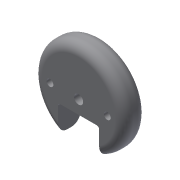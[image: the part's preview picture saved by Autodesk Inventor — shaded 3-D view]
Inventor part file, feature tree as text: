
AUTODESK INVENTOR PART (.ipt)
format: ipt  version: 2015 (Build 190159000, 159)  size: 184,320 bytes
history: native  units: mm
features: sketch x12, extrude x10, fillet x2
ambient origin geometry x8: Origin, YZ Plane, XZ Plane, XY Plane, X Axis, Y Axis, Z Axis, Center Point
bodies: Solid1 (feature_tree)
feature tree (24):
  extrude  "Extrusion1"  Depth=10.0mm TaperAngle=0.0deg
  extrude  "Extrusion2"  Depth=10.0mm TaperAngle=0.0deg
  extrude  "Extrusion3"  Depth=3.0mm
  sketch  "Sketch4"  dims[d9=10.0mm d10=0.0mm d11=10.0mm]
  sketch  "Sketch5"  dims[d12=10.0mm d13=0.0mm d14=6.0mm]
  extrude  "Extrusion4"  Depth=10.0mm
  extrude  "Extrusion5"  Depth=6.0mm
  extrude  "Extrusion6"  Depth=18.0mm
  extrude  "Extrusion7"  Depth=10.0mm TaperAngle=0.0deg
  extrude  "Extrusion8"  Depth=2.0mm
  extrude  "Extrusion9"  Depth=8.0mm TaperAngle=0.0deg
  extrude  "Extrusion10"  Depth=4.0mm
  fillet  "Fillet1"  Radius=10.0mm
  fillet  "Fillet2"  Radius=1.0mm
  sketch  "Sketch1"  dims[d0=40.0mm d1=10.0mm d2=0.0mm]
  sketch  "Sketch2"  dims[d3=12.0mm d4=10.0mm d5=0.0mm]
  sketch  "Sketch3"  dims[d7=3.0mm d8=3.0mm]
  sketch  "Sketch6"  dims[d15=2.0mm d16=0.0mm d17=18.0mm]
  sketch  "Sketch7"  dims[d18=10.0mm d19=10.0mm d20=0.0mm]
  sketch  "Sketch8"  dims[d21=18.0mm d25=2.0mm]
  sketch  "Sketch9"  dims[d26=10.0mm d27=0.0mm d28=8.0mm d29=0.0mm]
  sketch  "Sketch10"  dims[d30=8.0mm d31=0.0mm d32=4.0mm d33=10.0mm d34=0.0mm d35=1.0mm]
  sketch  "Sketch11"  dims[d36=4.0mm]
  sketch  "Sketch12"
